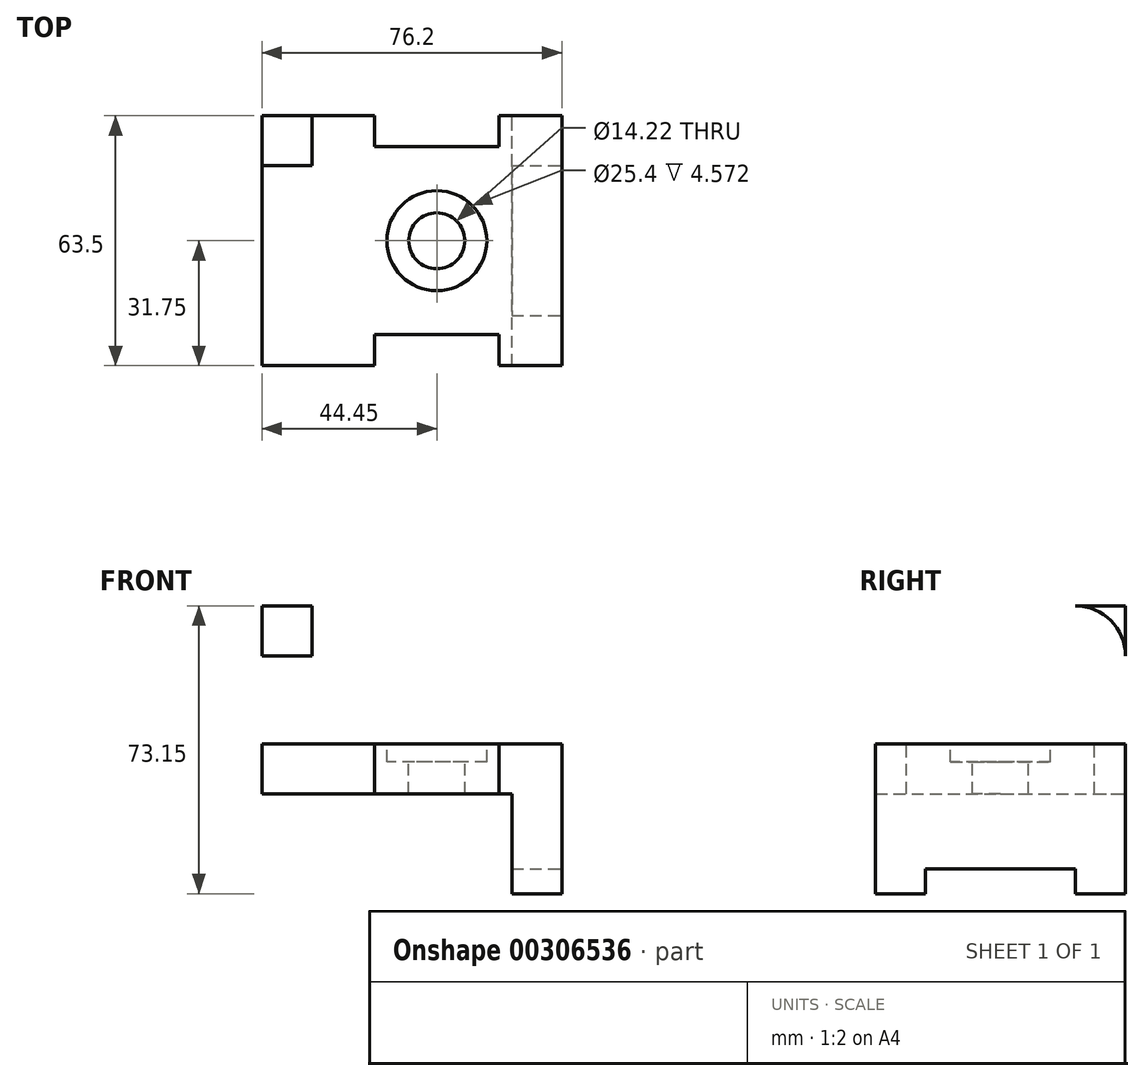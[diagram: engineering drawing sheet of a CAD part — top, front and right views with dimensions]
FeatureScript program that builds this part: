
annotation { "Feature Type Name" : "Feature", "Feature Type Description" : "" }
export const myFeature = defineFeature(function(context is Context, id is Id, definition is map)
    precondition{}
    {
        {
            var Q0;
            Q0=qCreatedBy(makeId("Front.planeOp"),FACE);
            var sketch = newSketch(context, id + "F0", { "sketchPlane" : qUnion([Q0])});
            skLineSegment(sketch, "E0", {"start": v(0, 0) * mm, "end": v(0, 47.75) * mm});
            skLineSegment(sketch, "E1", {"start": v(0, 47.75) * mm, "end": v(12.7, 47.75) * mm});
            skLineSegment(sketch, "E2", {"start": v(12.7, 47.75) * mm, "end": v(12.7, 12.7) * mm});
            skLineSegment(sketch, "E3", {"start": v(12.7, 12.7) * mm, "end": v(76.2, 12.7) * mm});
            skLineSegment(sketch, "E4", {"start": v(76.2, 12.7) * mm, "end": v(76.2, -25.4) * mm});
            skLineSegment(sketch, "E5", {"start": v(76.2, -25.4) * mm, "end": v(63.5, -25.4) * mm});
            skLineSegment(sketch, "E6", {"start": v(63.5, -25.4) * mm, "end": v(63.5, 0) * mm});
            skLineSegment(sketch, "E7", {"start": v(63.5, 0) * mm, "end": v(60.2, 0) * mm});
            skLineSegment(sketch, "E8", {"start": v(60.2, 0) * mm, "end": v(0, 0) * mm});
            skLineSegment(sketch, "E9", {"start": v(60.2, 0) * mm, "end": v(60.2, 12.7) * mm});
            skLineSegment(sketch, "E10", {"start": v(28.7, 0) * mm, "end": v(28.7, 12.7) * mm});
            skSolve(sketch);
        }
        {
            var Q0;
            {var subQ0=sQuery(id+"F0.wireOp",EDGE,"E9");Q0=makeQuery(id+"F0.imprint","IMPRINT",FACE,{"disambiguationData":[TD([[makeQuery(id+"F0.imprint","IMPRINT",EDGE,{"derivedFrom":subQ0}),1.0]])]});}
            extrude(context, id + "F1", {"entities" : qUnion([Q0]), "endBound" : BoundingType.SYMMETRIC, "depth" : 47.75 * mm});
        }
        {
            var Q0;
            {var subQ3=sQuery(id+"F0.wireOp",EDGE,"E0");Q0=makeQuery(id+"F0.imprint","IMPRINT",FACE,{"disambiguationData":[TD([[makeQuery(id+"F0.imprint","IMPRINT",EDGE,{"derivedFrom":subQ3}),-1.0]])]});}
            var Q1;
            {var subQ0=sQuery(id+"F0.wireOp",EDGE,"E4");Q1=makeQuery(id+"F0.imprint","IMPRINT",FACE,{"disambiguationData":[TD([[makeQuery(id+"F0.imprint","IMPRINT",EDGE,{"derivedFrom":subQ0}),-1.0]])]});}
            extrude(context, id + "F2", {"entities" : qUnion([Q0, Q1]), "operationType" : NewBodyOperationType.ADD, "endBound" : BoundingType.SYMMETRIC, "depth" : 63.5 * mm});
        }
        {
            var Q0;
            Q0=makeQuery(id+"F2.opExtrude","SWEPT_FACE",FACE,{"disambiguationData":[OSD([sQuery(id+"F0.wireOp",EDGE,"E4")])]});
            var sketch = newSketch(context, id + "F3", { "sketchPlane" : qUnion([Q0])});
            skLineSegment(sketch, "E11", {"start": v(-19.05, -25.4) * mm, "end": v(-19.05, -19.05) * mm});
            skLineSegment(sketch, "E12", {"start": v(-19.05, -19.05) * mm, "end": v(19.05, -19.05) * mm});
            skLineSegment(sketch, "E13", {"start": v(19.05, -19.05) * mm, "end": v(19.05, -25.4) * mm});
            skSolve(sketch);
        }
        {
            var Q0;
            {var subQ0=sQuery(id+"F3.wireOp",EDGE,"E11");Q0=makeQuery(id+"F3.imprint","IMPRINT",FACE,{"disambiguationData":[TD([[makeQuery(id+"F3.imprint","IMPRINT",EDGE,{"derivedFrom":subQ0}),-1.0]])]});}
            extrude(context, id + "F4", {"entities" : qUnion([Q0]), "operationType" : NewBodyOperationType.REMOVE, "endBound" : BoundingType.THROUGH_ALL, "oppositeDirection" : true, "depth" : 25.4 * mm});
        }
        {
            var Q0;
            Q0=makeQuery(id+"F2.opExtrude","SWEPT_FACE",FACE,{"disambiguationData":[OSD([sQuery(id+"F0.wireOp",EDGE,"E2")])]});
            var sketch = newSketch(context, id + "F5", { "sketchPlane" : qUnion([Q0])});
            skLineSegment(sketch, "E14", {"start": v(-19.05, 42.93) * mm, "end": v(19.05, 42.93) * mm});
            skLineSegment(sketch, "E15", {"start": v(-19.05, 27.18) * mm, "end": v(19.05, 27.18) * mm});
            skArc(sketch, "E16", {"start": v(-19.05, 42.93) * mm, "mid": v(-26.92, 35.05) * mm, "end": v(-19.05, 27.18) * mm});
            skArc(sketch, "E17", {"start": v(19.05, 27.18) * mm, "mid": v(26.92, 35.05) * mm, "end": v(19.05, 42.93) * mm});
            skArc(sketch, "E18", {"start": v(-19.05, 47.75) * mm, "mid": v(-28.03, 44.03) * mm, "end": v(-31.75, 35.05) * mm});
            skArc(sketch, "E19", {"start": v(19.05, 47.75) * mm, "mid": v(28.03, 44.03) * mm, "end": v(31.75, 35.05) * mm});
            skSolve(sketch);
        }
        {
            var Q0;
            {var subQ0=sQuery(id+"F5.wireOp",EDGE,"E18");Q0=makeQuery(id+"F5.imprint","IMPRINT",FACE,{"disambiguationData":[TD([[makeQuery(id+"F5.imprint","IMPRINT",EDGE,{"derivedFrom":subQ0}),-1.0]])]});}
            var Q1;
            Q1=makeQuery(id+"F5.imprint","IMPRINT",FACE,{"disambiguationData":[TD([[makeQuery(id+"F5.imprint","IMPRINT",EDGE,{"derivedFrom":sQuery(id+"F5.wireOp",EDGE,"E14")}),-1.0]])]});
            var Q2;
            {var subQ0=sQuery(id+"F5.wireOp",EDGE,"E19");Q2=makeQuery(id+"F5.imprint","IMPRINT",FACE,{"disambiguationData":[TD([[makeQuery(id+"F5.imprint","IMPRINT",EDGE,{"derivedFrom":subQ0}),1.0]])]});}
            extrude(context, id + "F6", {"entities" : qUnion([Q0, Q1, Q2]), "operationType" : NewBodyOperationType.REMOVE, "oppositeDirection" : true, "depth" : 25.4 * mm});
        }
        {
            var Q0;
            {var subQ0=sQuery(id+"F0.wireOp",EDGE,"E3");Q0=makeQuery(id+"F2.boolean.opBoolean","MERGE",FACE,{"derivedFrom":[makeQuery(id+"F1.opExtrude","SWEPT_FACE",FACE,{"disambiguationData":[OSD([subQ0])]}),makeQuery(id+"F2.opExtrude","SWEPT_FACE",FACE,{"disambiguationData":[OSD([subQ0]),TDD([makeQuery(id+"F0.imprint","IMPRINT",EDGE,{"disambiguationData":[TD([[makeQuery(id+"F0.imprint","INTERSECT",VERTEX,{"derivedFrom":[sQuery(id+"F0.wireOp",EDGE,"E2"),subQ0]}),-1.0]])],"derivedFrom":subQ0})])]}),makeQuery(id+"F2.opExtrude","SWEPT_FACE",FACE,{"disambiguationData":[OSD([subQ0]),TDD([makeQuery(id+"F0.imprint","IMPRINT",EDGE,{"disambiguationData":[TD([[makeQuery(id+"F0.imprint","INTERSECT",VERTEX,{"derivedFrom":[subQ0,sQuery(id+"F0.wireOp",EDGE,"E4")]}),1.0]])],"derivedFrom":subQ0})])]})]});}
            var sketch = newSketch(context, id + "F7", { "sketchPlane" : qUnion([Q0])});
            skCircle(sketch, "E20", {"center": v(44.45, 0) * mm, "radius": 12.7 * mm});
            skCircle(sketch, "E21", {"center": v(44.45, 0) * mm, "radius": 7.11 * mm});
            skSolve(sketch);
        }
        {
            var Q0;
            Q0=makeQuery(id+"F7.imprint","IMPRINT",FACE,{"disambiguationData":[TD([[makeQuery(id+"F7.imprint","IMPRINT",EDGE,{"derivedFrom":sQuery(id+"F7.wireOp",EDGE,"E21")}),1.0]])]});
            extrude(context, id + "F8", {"entities" : qUnion([Q0]), "operationType" : NewBodyOperationType.REMOVE, "endBound" : BoundingType.THROUGH_ALL, "oppositeDirection" : true, "depth" : 25.4 * mm});
        }
        {
            var Q0;
            Q0=makeQuery(id+"F7.imprint","IMPRINT",FACE,{"disambiguationData":[TD([[makeQuery(id+"F7.imprint","IMPRINT",EDGE,{"derivedFrom":sQuery(id+"F7.wireOp",EDGE,"E20")}),1.0]])]});
            extrude(context, id + "F9", {"entities" : qUnion([Q0]), "operationType" : NewBodyOperationType.REMOVE, "oppositeDirection" : true, "depth" : 4.57 * mm});
        }
    });
